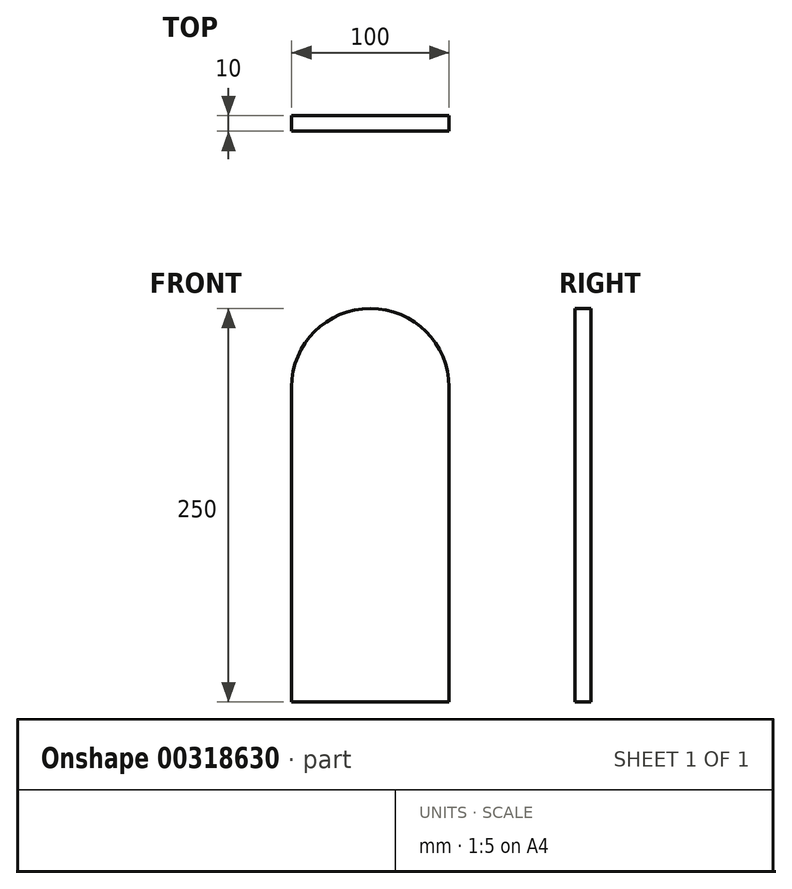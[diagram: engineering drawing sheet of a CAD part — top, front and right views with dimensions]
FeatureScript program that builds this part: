
annotation { "Feature Type Name" : "Feature", "Feature Type Description" : "" }
export const myFeature = defineFeature(function(context is Context, id is Id, definition is map)
    precondition{}
    {
        {
            var Q0;
            Q0=qCreatedBy(makeId("Front.planeOp"),FACE);
            var sketch = newSketch(context, id + "F0", { "sketchPlane" : qUnion([Q0])});
            skLineSegment(sketch, "E0", {"start": v(0, 0) * mm, "end": v(50, 0) * mm});
            skLineSegment(sketch, "E1", {"start": v(50, 0) * mm, "end": v(50, 200) * mm});
            skLineSegment(sketch, "E2.MirrorCS", {"start": v(0, 0) * mm, "end": v(-50, 0) * mm});
            skLineSegment(sketch, "E3.MirrorCS", {"start": v(-50, 0) * mm, "end": v(-50, 200) * mm});
            skArc(sketch, "E4", {"start": v(50, 200) * mm, "mid": v(0, 250) * mm, "end": v(-50, 200) * mm});
            skSolve(sketch);
        }
        {
            var Q0;
            Q0=makeQuery(id+"F0.imprint","IMPRINT",FACE,{"disambiguationData":[TD([[makeQuery(id+"F0.imprint","IMPRINT",EDGE,{"derivedFrom":sQuery(id+"F0.wireOp",EDGE,"E0")}),1.0]])]});
            extrude(context, id + "F1", {"entities" : qUnion([Q0]), "depth" : 10 * mm});
        }
    });
